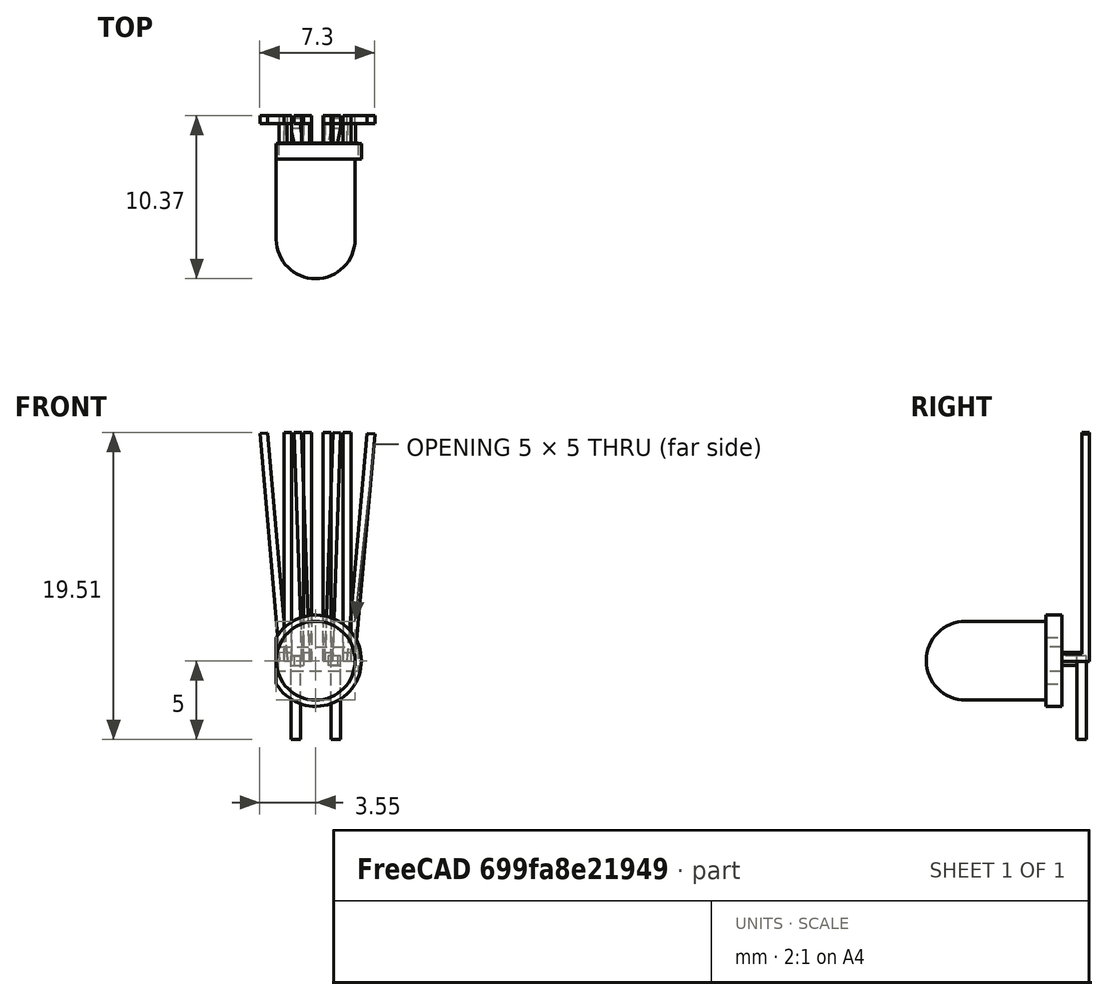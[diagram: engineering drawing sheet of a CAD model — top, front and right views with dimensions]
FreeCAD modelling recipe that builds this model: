
FCSTD DOCUMENT  (FreeCAD 0.20R29410 (Git))
Label: np_led
License: All rights reserved
LicenseURL: http://en.wikipedia.org/wiki/All_rights_reserved
objects: Sketcher::SketchObject×10, PartDesign::Pad×10, Part::Feature×2, PartDesign::Body×2, App::VRMLObject×1, Mesh::Feature×1
note: 34 computed .brp shape members not serialized (recipe doc carries the construction recipe); baked Part::Feature solids carry a one-line shape summary decoded from their .brp

FEATURE [Part::Feature] Part__Feature  label="LED_D5.0mm_Horizontal_O1.27mm_Z3.0mm_Clear"
  shape: bbox 5.4 x 10.17 x 7.9 mm, 33 faces (baked)
FEATURE [App::VRMLObject] LED_D5
FEATURE [Mesh::Feature] Mesh  label="LED_D5.0mm_Horizontal_O1.27mm_Z3.0mm_Clear (Meshed)"
FEATURE [Sketcher::SketchObject] Sketch
  AttachmentOffset = pos=(0,0,-0.75) rot=(0,0,1;0rad)
  FullyConstrained = false
  MapMode = 5
  Placement = pos=(-0.75,2e-16,-2e-16) rot=(0.57735,0.57735,0.57735;2.0944rad)
  Support = -> [YZ_Plane]
  sketch-geometry (6):
    g0: LineSegment StartX=-1.5 StartY=3 StartZ=0 EndX=0.5 EndY=3 EndZ=0
    g1: LineSegment StartX=0.5 StartY=3 StartZ=0 EndX=0.5 EndY=17.5 EndZ=0
    g2: LineSegment StartX=0.5 StartY=17.5 StartZ=0 EndX=0 EndY=17.5 EndZ=0
    g3: LineSegment StartX=0 StartY=17.5 StartZ=0 EndX=0 EndY=3.5 EndZ=0
    g4: LineSegment StartX=0 StartY=3.5 StartZ=0 EndX=-1.5 EndY=3.5 EndZ=0
    g5: LineSegment StartX=-1.5 StartY=3.5 StartZ=0 EndX=-1.5 EndY=3 EndZ=0
  constraints (13):
    c: Horizontal(g0)
    c: Coincident(g0,g1)
    c: Vertical(g1)
    c: Coincident(g1,g2)
    c: PointOnObject(g2,g-2)
    c: Horizontal(g2)
    c: Coincident(g2,g3)
    c: PointOnObject(g3,g-2)
    c: Coincident(g3,g4)
    c: Horizontal(g4)
    c: Coincident(g4,g5)
    c: Coincident(g5,g0)
    c: Vertical(g5)
FEATURE [Sketcher::SketchObject] Sketch001
  AttachmentOffset = pos=(0,0,0.5) rot=(0,0,1;0rad)
  FullyConstrained = false
  MapMode = 5
  Placement = pos=(0.5,-1e-16,1e-16) rot=(0.57735,0.57735,0.57735;2.0944rad)
  Support = -> [YZ_Plane]
  sketch-geometry (6):
    g0: LineSegment StartX=-1.5 StartY=3 StartZ=0 EndX=0.5 EndY=3 EndZ=0
    g1: LineSegment StartX=0.5 StartY=3 StartZ=0 EndX=0.5 EndY=17.5 EndZ=0
    g2: LineSegment StartX=0.5 StartY=17.5 StartZ=0 EndX=0 EndY=17.5 EndZ=0
    g3: LineSegment StartX=0 StartY=17.5 StartZ=0 EndX=0 EndY=3.5 EndZ=0
    g4: LineSegment StartX=0 StartY=3.5 StartZ=0 EndX=-1.5 EndY=3.5 EndZ=0
    g5: LineSegment StartX=-1.5 StartY=3.5 StartZ=0 EndX=-1.5 EndY=3 EndZ=0
  constraints (13):
    c: Horizontal(g0)
    c: Coincident(g0,g1)
    c: Vertical(g1)
    c: Coincident(g1,g2)
    c: PointOnObject(g2,g-2)
    c: Horizontal(g2)
    c: Coincident(g2,g3)
    c: PointOnObject(g3,g-2)
    c: Coincident(g3,g4)
    c: Horizontal(g4)
    c: Coincident(g4,g5)
    c: Coincident(g5,g0)
    c: Vertical(g5)
FEATURE [Sketcher::SketchObject] Sketch002
  AttachmentOffset = pos=(0,0,1.75) rot=(0,0,1;0rad)
  FullyConstrained = false
  MapMode = 5
  Placement = pos=(1.75,-4e-16,4e-16) rot=(0.57735,0.57735,0.57735;2.0944rad)
  Support = -> [YZ_Plane]
  sketch-geometry (6):
    g0: LineSegment StartX=-1.5 StartY=3 StartZ=0 EndX=0.5 EndY=3 EndZ=0
    g1: LineSegment StartX=0.5 StartY=3 StartZ=0 EndX=0.5 EndY=17.5 EndZ=0
    g2: LineSegment StartX=0.5 StartY=17.5 StartZ=0 EndX=0 EndY=17.5 EndZ=0
    g3: LineSegment StartX=0 StartY=17.5 StartZ=0 EndX=0 EndY=3.5 EndZ=0
    g4: LineSegment StartX=0 StartY=3.5 StartZ=0 EndX=-1.5 EndY=3.5 EndZ=0
    g5: LineSegment StartX=-1.5 StartY=3.5 StartZ=0 EndX=-1.5 EndY=3 EndZ=0
  constraints (13):
    c: Horizontal(g0)
    c: Coincident(g0,g1)
    c: Vertical(g1)
    c: Coincident(g1,g2)
    c: PointOnObject(g2,g-2)
    c: Horizontal(g2)
    c: Coincident(g2,g3)
    c: PointOnObject(g3,g-2)
    c: Coincident(g3,g4)
    c: Horizontal(g4)
    c: Coincident(g4,g5)
    c: Coincident(g5,g0)
    c: Vertical(g5)
FEATURE [Sketcher::SketchObject] Sketch003
  AttachmentOffset = pos=(0,0,3) rot=(0,0,1;0rad)
  FullyConstrained = false
  MapMode = 5
  Placement = pos=(3,-7e-16,7e-16) rot=(0.57735,0.57735,0.57735;2.0944rad)
  Support = -> [YZ_Plane]
  sketch-geometry (6):
    g0: LineSegment StartX=-1.5 StartY=3 StartZ=0 EndX=0.5 EndY=3 EndZ=0
    g1: LineSegment StartX=0.5 StartY=3 StartZ=0 EndX=0.5 EndY=17.5 EndZ=0
    g2: LineSegment StartX=0.5 StartY=17.5 StartZ=0 EndX=0 EndY=17.5 EndZ=0
    g3: LineSegment StartX=0 StartY=17.5 StartZ=0 EndX=0 EndY=3.5 EndZ=0
    g4: LineSegment StartX=0 StartY=3.5 StartZ=0 EndX=-1.5 EndY=3.5 EndZ=0
    g5: LineSegment StartX=-1.5 StartY=3.5 StartZ=0 EndX=-1.5 EndY=3 EndZ=0
  constraints (13):
    c: Horizontal(g0)
    c: Coincident(g0,g1)
    c: Vertical(g1)
    c: Coincident(g1,g2)
    c: PointOnObject(g2,g-2)
    c: Horizontal(g2)
    c: Coincident(g2,g3)
    c: PointOnObject(g3,g-2)
    c: Coincident(g3,g4)
    c: Horizontal(g4)
    c: Coincident(g4,g5)
    c: Coincident(g5,g0)
    c: Vertical(g5)
FEATURE [Sketcher::SketchObject] Sketch004
  AttachmentOffset = pos=(0,0,1.25) rot=(0,0,1;0rad)
  FullyConstrained = false
  MapMode = 5
  Placement = pos=(0,-1.25,-3e-16) rot=(1,0,0;1.5708rad)
  Support = -> [XZ_Plane]
  sketch-geometry (4):
    g0: LineSegment StartX=-1.07321 StartY=3.86447 StartZ=0 EndX=3.94656 EndY=3.86447 EndZ=0
    g1: LineSegment StartX=3.94656 StartY=3.86447 StartZ=0 EndX=3.94656 EndY=2.30344 EndZ=0
    g2: LineSegment StartX=3.94656 StartY=2.30344 StartZ=0 EndX=-1.07321 EndY=2.30344 EndZ=0
    g3: LineSegment StartX=-1.07321 StartY=2.30344 StartZ=0 EndX=-1.07321 EndY=3.86447 EndZ=0
  constraints (8):
    c: Coincident(g0,g1)
    c: Coincident(g1,g2)
    c: Coincident(g2,g3)
    c: Coincident(g3,g0)
    c: Horizontal(g0)
    c: Horizontal(g2)
    c: Vertical(g1)
    c: Vertical(g3)
FEATURE [PartDesign::Pad] Pad002
  Direction = (0,-1,2e-16)
  Length = 1
  Length2 = 10
  Placement = pos=(0,0,0) rot=(1,0,0;1.5708rad)
  Profile = -> Sketch004
  ReferenceAxis = -> Sketch004 [N_Axis]
  Type = 0
FEATURE [PartDesign::Pad] Pad
  BaseFeature = -> Pad002
  Direction = (1,-2e-16,3e-16)
  Length = 0.5
  Length2 = 10
  Placement = pos=(0,0,0) rot=(1,0,0;1.5708rad)
  Profile = -> Sketch
  ReferenceAxis = -> Sketch [N_Axis]
  Type = 0
FEATURE [PartDesign::Pad] Pad001
  BaseFeature = -> Pad
  Direction = (1,-2e-16,3e-16)
  Length = 0.5
  Length2 = 10
  Placement = pos=(0,0,0) rot=(1,0,0;1.5708rad)
  Profile = -> Sketch001
  ReferenceAxis = -> Sketch001 [N_Axis]
  Type = 0
FEATURE [PartDesign::Pad] Pad003
  BaseFeature = -> Pad001
  Direction = (1,-2e-16,3e-16)
  Length = 0.5
  Length2 = 10
  Placement = pos=(0,0,0) rot=(1,0,0;1.5708rad)
  Profile = -> Sketch002
  ReferenceAxis = -> Sketch002 [N_Axis]
  Type = 0
FEATURE [PartDesign::Pad] Pad004
  BaseFeature = -> Pad003
  Direction = (1,-2e-16,3e-16)
  Length = 0.5
  Length2 = 10
  Placement = pos=(0,0,0) rot=(1,0,0;1.5708rad)
  Profile = -> Sketch003
  ReferenceAxis = -> Sketch003 [N_Axis]
  Type = 0
FEATURE [PartDesign::Body] Body
  Group = -> [Pad002,Sketch,Pad,Sketch001,Sketch002,Sketch003,Pad001,Sketch004,Pad003,Pad004]
  Origin = -> Origin
  Tip = -> Pad004
FEATURE [Part::Feature] Mesh001
  shape: bbox 5.4 x 8.6 x 5.799 mm, 1742 faces, 0 solids (baked)
FEATURE [Sketcher::SketchObject] Sketch005
  AttachmentOffset = pos=(0,0,-0.75) rot=(1,0,0;-0.087266rad)
  FullyConstrained = false
  MapMode = 5
  Placement = pos=(-0.75,2e-16,-2e-16) rot=(-0.559809,-0.559809,-0.610924;4.23842rad)
  Support = -> [YZ_Plane001]
  sketch-geometry (6):
    g0: LineSegment StartX=-1.5 StartY=3 StartZ=0 EndX=0.5 EndY=3 EndZ=0
    g1: LineSegment StartX=0.5 StartY=3 StartZ=0 EndX=0.5 EndY=17.5 EndZ=0
    g2: LineSegment StartX=0.5 StartY=17.5 StartZ=0 EndX=0 EndY=17.5 EndZ=0
    g3: LineSegment StartX=0 StartY=17.5 StartZ=0 EndX=0 EndY=3.5 EndZ=0
    g4: LineSegment StartX=0 StartY=3.5 StartZ=0 EndX=-1.5 EndY=3.5 EndZ=0
    g5: LineSegment StartX=-1.5 StartY=3.5 StartZ=0 EndX=-1.5 EndY=3 EndZ=0
  constraints (13):
    c: Horizontal(g0)
    c: Coincident(g0,g1)
    c: Vertical(g1)
    c: Coincident(g1,g2)
    c: PointOnObject(g2,g-2)
    c: Horizontal(g2)
    c: Coincident(g2,g3)
    c: PointOnObject(g3,g-2)
    c: Coincident(g3,g4)
    c: Horizontal(g4)
    c: Coincident(g4,g5)
    c: Coincident(g5,g0)
    c: Vertical(g5)
FEATURE [Sketcher::SketchObject] Sketch006
  AttachmentOffset = pos=(0,0,0.5) rot=(1,0,0;-0.034907rad)
  FullyConstrained = false
  MapMode = 5
  Placement = pos=(0.5,-1e-16,1e-16) rot=(-0.570514,-0.570514,-0.590785;4.20883rad)
  Support = -> [YZ_Plane001]
  sketch-geometry (6):
    g0: LineSegment StartX=-1.5 StartY=3 StartZ=0 EndX=0.5 EndY=3 EndZ=0
    g1: LineSegment StartX=0.5 StartY=3 StartZ=0 EndX=0.5 EndY=17.5 EndZ=0
    g2: LineSegment StartX=0.5 StartY=17.5 StartZ=0 EndX=0 EndY=17.5 EndZ=0
    g3: LineSegment StartX=0 StartY=17.5 StartZ=0 EndX=0 EndY=3.5 EndZ=0
    g4: LineSegment StartX=0 StartY=3.5 StartZ=0 EndX=-1.5 EndY=3.5 EndZ=0
    g5: LineSegment StartX=-1.5 StartY=3.5 StartZ=0 EndX=-1.5 EndY=3 EndZ=0
  constraints (13):
    c: Horizontal(g0)
    c: Coincident(g0,g1)
    c: Vertical(g1)
    c: Coincident(g1,g2)
    c: PointOnObject(g2,g-2)
    c: Horizontal(g2)
    c: Coincident(g2,g3)
    c: PointOnObject(g3,g-2)
    c: Coincident(g3,g4)
    c: Horizontal(g4)
    c: Coincident(g4,g5)
    c: Coincident(g5,g0)
    c: Vertical(g5)
FEATURE [Sketcher::SketchObject] Sketch007
  AttachmentOffset = pos=(0,0,1.75) rot=(1,0,0;0.034907rad)
  FullyConstrained = false
  MapMode = 5
  Placement = pos=(1.75,-4e-16,4e-16) rot=(0.583952,0.583952,0.563916;2.11466rad)
  Support = -> [YZ_Plane001]
  sketch-geometry (6):
    g0: LineSegment StartX=-1.5 StartY=3 StartZ=0 EndX=0.5 EndY=3 EndZ=0
    g1: LineSegment StartX=0.5 StartY=3 StartZ=0 EndX=0.5 EndY=17.5 EndZ=0
    g2: LineSegment StartX=0.5 StartY=17.5 StartZ=0 EndX=0 EndY=17.5 EndZ=0
    g3: LineSegment StartX=0 StartY=17.5 StartZ=0 EndX=0 EndY=3.5 EndZ=0
    g4: LineSegment StartX=0 StartY=3.5 StartZ=0 EndX=-1.5 EndY=3.5 EndZ=0
    g5: LineSegment StartX=-1.5 StartY=3.5 StartZ=0 EndX=-1.5 EndY=3 EndZ=0
  constraints (13):
    c: Horizontal(g0)
    c: Coincident(g0,g1)
    c: Vertical(g1)
    c: Coincident(g1,g2)
    c: PointOnObject(g2,g-2)
    c: Horizontal(g2)
    c: Coincident(g2,g3)
    c: PointOnObject(g3,g-2)
    c: Coincident(g3,g4)
    c: Horizontal(g4)
    c: Coincident(g4,g5)
    c: Coincident(g5,g0)
    c: Vertical(g5)
FEATURE [Sketcher::SketchObject] Sketch008
  AttachmentOffset = pos=(0,0,3) rot=(1,0,0;0.087266rad)
  FullyConstrained = false
  MapMode = 5
  Placement = pos=(3,-7e-16,7e-16) rot=(0.593426,0.593426,0.543775;2.14549rad)
  Support = -> [YZ_Plane001]
  sketch-geometry (6):
    g0: LineSegment StartX=-1.5 StartY=3 StartZ=0 EndX=0.5 EndY=3 EndZ=0
    g1: LineSegment StartX=0.5 StartY=3 StartZ=0 EndX=0.5 EndY=17.5 EndZ=0
    g2: LineSegment StartX=0.5 StartY=17.5 StartZ=0 EndX=0 EndY=17.5 EndZ=0
    g3: LineSegment StartX=0 StartY=17.5 StartZ=0 EndX=0 EndY=3.5 EndZ=0
    g4: LineSegment StartX=0 StartY=3.5 StartZ=0 EndX=-1.5 EndY=3.5 EndZ=0
    g5: LineSegment StartX=-1.5 StartY=3.5 StartZ=0 EndX=-1.5 EndY=3 EndZ=0
  constraints (13):
    c: Horizontal(g0)
    c: Coincident(g0,g1)
    c: Vertical(g1)
    c: Coincident(g1,g2)
    c: PointOnObject(g2,g-2)
    c: Horizontal(g2)
    c: Coincident(g2,g3)
    c: PointOnObject(g3,g-2)
    c: Coincident(g3,g4)
    c: Horizontal(g4)
    c: Coincident(g4,g5)
    c: Coincident(g5,g0)
    c: Vertical(g5)
FEATURE [Sketcher::SketchObject] Sketch009
  AttachmentOffset = pos=(0,0,1.25) rot=(0,0,1;0rad)
  FullyConstrained = false
  MapMode = 5
  Placement = pos=(0,-1.25,-3e-16) rot=(1,0,0;1.5708rad)
  Support = -> [XZ_Plane001]
  sketch-geometry (4):
    g0: LineSegment StartX=-1.07321 StartY=3.86447 StartZ=0 EndX=3.94656 EndY=3.86447 EndZ=0
    g1: LineSegment StartX=3.94656 StartY=3.86447 StartZ=0 EndX=3.94656 EndY=2.30344 EndZ=0
    g2: LineSegment StartX=3.94656 StartY=2.30344 StartZ=0 EndX=-1.07321 EndY=2.30344 EndZ=0
    g3: LineSegment StartX=-1.07321 StartY=2.30344 StartZ=0 EndX=-1.07321 EndY=3.86447 EndZ=0
  constraints (8):
    c: Coincident(g0,g1)
    c: Coincident(g1,g2)
    c: Coincident(g2,g3)
    c: Coincident(g3,g0)
    c: Horizontal(g0)
    c: Horizontal(g2)
    c: Vertical(g1)
    c: Vertical(g3)
FEATURE [PartDesign::Pad] Pad007
  Direction = (0,-1,-2e-16)
  Length = 1
  Length2 = 10
  Placement = pos=(0,0,0) rot=(1,0,0;1.5708rad)
  Profile = -> Sketch009
  ReferenceAxis = -> Sketch009 [N_Axis]
  Type = 0
FEATURE [PartDesign::Pad] Pad005
  BaseFeature = -> Pad007
  Direction = (0.996195,-2e-16,0.0871557)
  Length = 0.5
  Length2 = 10
  Placement = pos=(0,0,0) rot=(1,0,0;1.5708rad)
  Profile = -> Sketch005
  ReferenceAxis = -> Sketch005 [N_Axis]
  Type = 0
FEATURE [PartDesign::Pad] Pad006
  BaseFeature = -> Pad005
  Direction = (0.999391,-2e-16,0.0348995)
  Length = 0.5
  Length2 = 10
  Placement = pos=(0,0,0) rot=(1,0,0;1.5708rad)
  Profile = -> Sketch006
  ReferenceAxis = -> Sketch006 [N_Axis]
  Type = 0
FEATURE [PartDesign::Pad] Pad008
  BaseFeature = -> Pad006
  Direction = (0.999391,-2e-16,-0.0348995)
  Length = 0.5
  Length2 = 10
  Placement = pos=(0,0,0) rot=(1,0,0;1.5708rad)
  Profile = -> Sketch007
  ReferenceAxis = -> Sketch007 [N_Axis]
  Type = 0
FEATURE [PartDesign::Pad] Pad009
  BaseFeature = -> Pad008
  Direction = (0.996195,-3e-16,-0.0871557)
  Length = 0.5
  Length2 = 10
  Placement = pos=(0,0,0) rot=(1,0,0;1.5708rad)
  Profile = -> Sketch008
  ReferenceAxis = -> Sketch008 [N_Axis]
  Type = 0
FEATURE [PartDesign::Body] Body001
  Group = -> [Pad007,Sketch005,Pad005,Sketch006,Sketch007,Sketch008,Pad006,Sketch009,Pad008,Pad009]
  Origin = -> Origin001
  Tip = -> Pad009
